# Revit family: CPR
name_source: partatom
category: Lighting Fixtures
revit_build: Autodesk Revit 2014 (Build: 20130308_1515(x64)
units: mm (PartAtom-declared; Revit-internal decimal feet)

## types (2) — shared parameters
Apparent Load = 4 VA
Certification = UL 924 Listed
NFPA 101 Life Safety Code
CEC T20 Compliant
Default Elevation = 48.000"
Description = Injection molded thermoplastic decorative lamphead and mounting plate
assembly. Mounts to 3½” octagonal or single gang boxes. Single and twin
lamp fixtures with MR16 lamp included. Standard finish is available in
white or black.
End = C2-End : C1
End-C1 = End : C1
Finish = Hubbell - White
Glass = Hubbell - light Glass
Holder Material = Hubbell - Steel
Lamp = Halogen MR16/ 3 Watt LED Lamp
Lens = Hubbell - Green Glass
Load Classification = Lighting
Manufacturer = DUAL-LITE
Model = CPR
Product Documentation Link = https://hubbellcdn.com
Product Page URL = https://www.hubbell.com
Type Comments = Emergency & Exit Lighting
URL = https://www.hubbell.com
Wall Plate Material = Hubbell - Black
Warranty = https://hubbellcdn.com
Wattage Comments = 3.72 W
Watts = 4 W

## per-type parameters (varying)
| type | Double Face | Ex 1 | Ex 2 | Single Face |
| CPR-S | No | 10.000" | 5.000" | Yes |
| CPR-D | Yes | 5.000" | 10.000" | No |

## geometry (parser evidence)
native form markers: Sweep x6
no freeform markers — native parametric forms only
